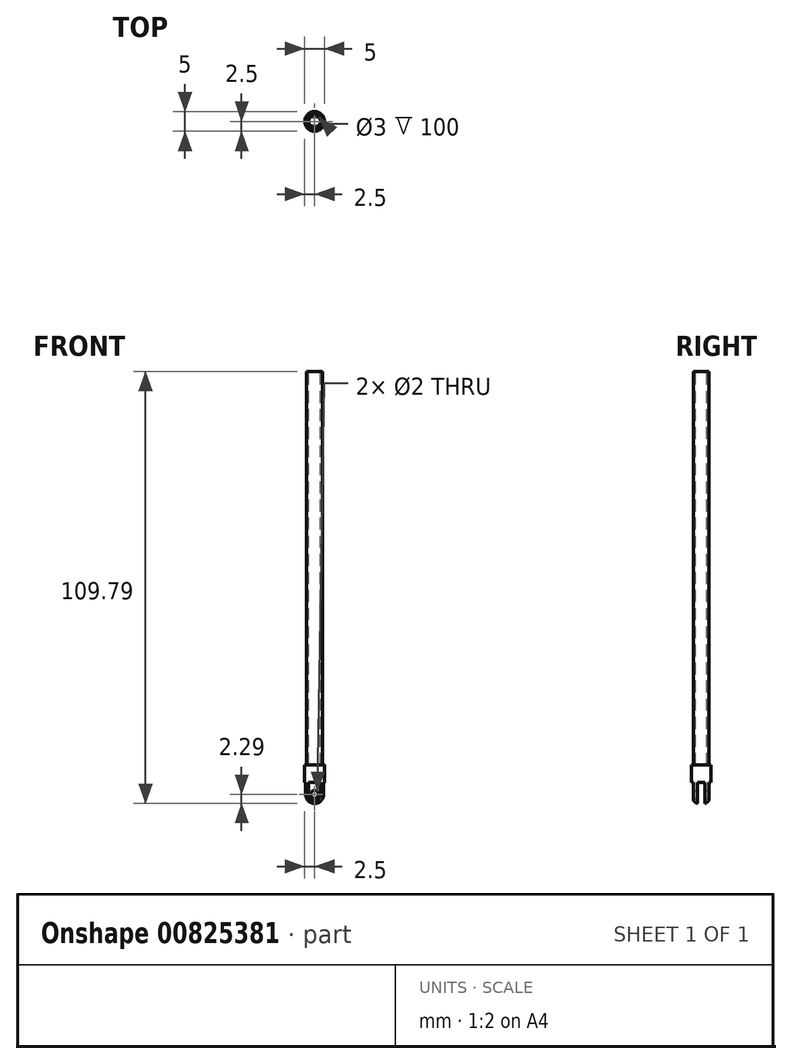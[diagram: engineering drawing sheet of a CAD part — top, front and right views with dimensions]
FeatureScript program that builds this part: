
annotation { "Feature Type Name" : "Feature", "Feature Type Description" : "" }
export const myFeature = defineFeature(function(context is Context, id is Id, definition is map)
    precondition{}
    {
        {
            var Q0;
            Q0=qCreatedBy(makeId("Top.planeOp"),FACE);
            var sketch = newSketch(context, id + "F0", { "sketchPlane" : qUnion([Q0])});
            skCircle(sketch, "E0", {"center": v(0, 0) * mm, "radius": 2 * mm});
            skSolve(sketch);
        }
        {
            var Q0;
            Q0 = qSketchRegion(id + "F0", true);
            extrude(context, id + "F1", {"entities" : qUnion([Q0]), "depth" : 100 * mm, "offsetDistance" : 25 * mm});
        }
        {
            var Q0;
            Q0=makeQuery(id+"F1.opExtrude","CAP_FACE",FACE,{"disambiguationData":[OSD([sQuery(id+"F0.wireOp",EDGE,"E0")])],"isStart":true});
            var sketch = newSketch(context, id + "F2", { "sketchPlane" : qUnion([Q0])});
            skCircle(sketch, "E1", {"center": v(0, 0) * mm, "radius": 2.5 * mm});
            skSolve(sketch);
        }
        {
            var Q0;
            Q0 = qSketchRegion(id + "F2", true);
            extrude(context, id + "F3", {"entities" : qUnion([Q0]), "operationType" : NewBodyOperationType.ADD, "depth" : 10 * mm, "offsetDistance" : 25 * mm});
        }
        {
            var Q0;
            Q0=makeQuery(id+"F3.opExtrude","CAP_EDGE",EDGE,{"disambiguationData":[OSD([sQuery(id+"F2.wireOp",EDGE,"E1")])],"isStart":false});
            fillet(context, id + "F4", {"entities" : qUnion([Q0]), "radius" : 2.5 * mm, "tangentPropagation" : true, "allowEdgeOverflow" : false});
        }
        {
            var Q0;
            Q0=qCreatedBy(makeId("Right.planeOp"),FACE);
            var sketch = newSketch(context, id + "F5", { "sketchPlane" : qUnion([Q0])});
            skLineSegment(sketch, "E2", {"start": v(0, -9.83) * mm, "end": v(0, -4.5) * mm, "construction": true});
            skLineSegment(sketch, "E3", {"start": v(0, -4.5) * mm, "end": v(1, -4.5) * mm, "construction": true});
            skLineSegment(sketch, "E4", {"start": v(0, -4.5) * mm, "end": v(-1, -4.5) * mm, "construction": true});
            skLineSegment(sketch, "E5.bottom", {"start": v(1, -4.5) * mm, "end": v(-1, -4.5) * mm});
            skLineSegment(sketch, "E5.top", {"start": v(1, -4.5) * mm, "end": v(-1, -4.5) * mm});
            skLineSegment(sketch, "E5.left", {"start": v(1, -4.5) * mm, "end": v(1, -4.5) * mm});
            skLineSegment(sketch, "E5.right", {"start": v(-1, -4.5) * mm, "end": v(-1, -4.5) * mm});
            skPoint(sketch, "E5.middle", {"position": v(0, -4.5) * mm});
            skLineSegment(sketch, "E6.bottom", {"start": v(-1, -4.5) * mm, "end": v(1, -4.5) * mm});
            skLineSegment(sketch, "E6.top", {"start": v(-1, -11.07) * mm, "end": v(1, -11.07) * mm});
            skLineSegment(sketch, "E6.left", {"start": v(-1, -4.5) * mm, "end": v(-1, -11.07) * mm});
            skLineSegment(sketch, "E6.right", {"start": v(1, -4.5) * mm, "end": v(1, -11.07) * mm});
            skLineSegment(sketch, "E7", {"start": v(1, -14.5) * mm, "end": v(2, -14.5) * mm, "construction": true});
            skLineSegment(sketch, "E8", {"start": v(-1, -14.5) * mm, "end": v(-2, -14.5) * mm, "construction": true});
            skPoint(sketch, "E9.oppositeSnap0", {"position": v(1.5, -14.5) * mm});
            skLineSegment(sketch, "E9.bottom", {"start": v(2, -4.5) * mm, "end": v(3.54, -4.5) * mm});
            skLineSegment(sketch, "E9.top", {"start": v(2, -14.5) * mm, "end": v(3.54, -14.5) * mm});
            skLineSegment(sketch, "E9.left", {"start": v(2, -4.5) * mm, "end": v(2, -14.5) * mm});
            skLineSegment(sketch, "E9.right", {"start": v(3.54, -4.5) * mm, "end": v(3.54, -14.5) * mm});
            skLineSegment(sketch, "E10.bottom", {"start": v(-2, -14.5) * mm, "end": v(-3.26, -14.5) * mm});
            skLineSegment(sketch, "E10.top", {"start": v(-2, -4.5) * mm, "end": v(-3.26, -4.5) * mm});
            skLineSegment(sketch, "E10.left", {"start": v(-2, -14.5) * mm, "end": v(-2, -4.5) * mm});
            skLineSegment(sketch, "E10.right", {"start": v(-3.26, -14.5) * mm, "end": v(-3.26, -4.5) * mm});
            skSolve(sketch);
        }
        {
            var Q0;
            Q0 = qSketchRegion(id + "F5", true);
            extrude(context, id + "F6", {"entities" : qUnion([Q0]), "operationType" : NewBodyOperationType.REMOVE, "endBound" : BoundingType.SYMMETRIC, "oppositeDirection" : true, "depth" : 25 * mm, "offsetDistance" : 25 * mm});
        }
        {
            var Q0;
            Q0=makeQuery(id+"F6.boolean.opBoolean","COPY",FACE,{"derivedFrom":makeQuery(id+"F6.opExtrude","SWEPT_FACE",FACE,{"disambiguationData":[OSD([sQuery(id+"F5.wireOp",EDGE,"E10.left")])]})});
            var sketch = newSketch(context, id + "F7", { "sketchPlane" : qUnion([Q0])});
            skCircle(sketch, "E11", {"center": v(0, -7.5) * mm, "radius": 1 * mm});
            skSolve(sketch);
        }
        {
            var Q0;
            Q0 = qSketchRegion(id + "F7", true);
            extrude(context, id + "F8", {"entities" : qUnion([Q0]), "operationType" : NewBodyOperationType.REMOVE, "endBound" : BoundingType.SYMMETRIC, "depth" : 25 * mm, "offsetDistance" : 25 * mm});
        }
        {
            var Q0;
            Q0=makeQuery(id+"F1.opExtrude","CAP_FACE",FACE,{"disambiguationData":[OSD([sQuery(id+"F0.wireOp",EDGE,"E0")])],"isStart":false});
            var sketch = newSketch(context, id + "F9", { "sketchPlane" : qUnion([Q0])});
            skCircle(sketch, "E12", {"center": v(0, 0) * mm, "radius": 1.5 * mm});
            skSolve(sketch);
        }
        {
            var Q0;
            Q0 = qSketchRegion(id + "F9", true);
            extrude(context, id + "F10", {"entities" : qUnion([Q0]), "operationType" : NewBodyOperationType.REMOVE, "oppositeDirection" : true, "depth" : 100 * mm, "offsetDistance" : 25 * mm});
        }
    });
